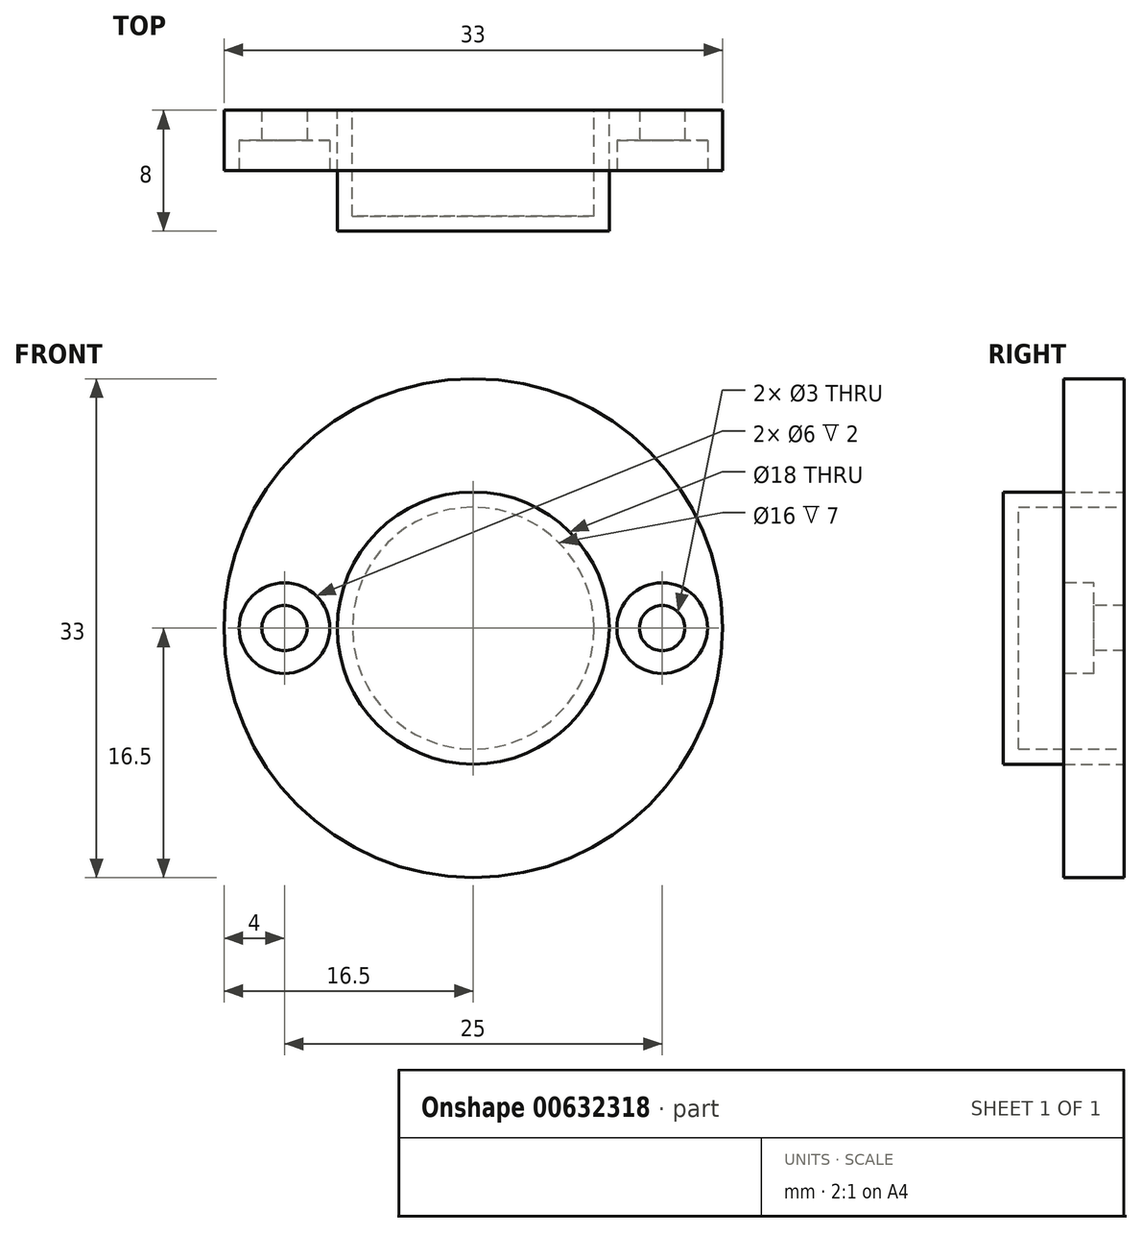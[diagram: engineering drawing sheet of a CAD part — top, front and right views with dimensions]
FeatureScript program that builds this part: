
annotation { "Feature Type Name" : "Feature", "Feature Type Description" : "" }
export const myFeature = defineFeature(function(context is Context, id is Id, definition is map)
    precondition{}
    {
        {
            var Q0;
            Q0=qCreatedBy(makeId("Front.planeOp"),FACE);
            var sketch = newSketch(context, id + "F0", { "sketchPlane" : qUnion([Q0])});
            skCircle(sketch, "E0", {"center": v(0, 0) * mm, "radius": 16.5 * mm});
            skPoint(sketch, "E1", {"position": v(-12.5, 0) * mm});
            skPoint(sketch, "E2", {"position": v(12.5, 0) * mm});
            skCircle(sketch, "E3", {"center": v(0, 0) * mm, "radius": 9 * mm});
            skSolve(sketch);
        }
        {
            var Q0;
            Q0=makeQuery(id+"F0.imprint","IMPRINT",FACE,{"disambiguationData":[TD([[makeQuery(id+"F0.imprint","IMPRINT",EDGE,{"derivedFrom":sQuery(id+"F0.wireOp",EDGE,"E3")}),1.0]])]});
            var Q1;
            Q1=sQuery(id+"F0.wireOp",EDGE,"E3");
            extrude(context, id + "F1", {"entities" : qUnion([Q0]), "surfaceEntities" : qUnion([Q1]), "depth" : 8 * mm, "offsetDistance" : 25 * mm});
        }
        {
            var Q0;
            Q0=makeQuery(id+"F0.imprint","IMPRINT",FACE,{"disambiguationData":[TD([[makeQuery(id+"F0.imprint","IMPRINT",EDGE,{"derivedFrom":sQuery(id+"F0.wireOp",EDGE,"E0")}),1.0]])]});
            var Q1;
            Q1=sQuery(id+"F0.wireOp",EDGE,"E0");
            extrude(context, id + "F2", {"entities" : qUnion([Q0]), "surfaceEntities" : qUnion([Q1]), "depth" : 4 * mm, "offsetDistance" : 25 * mm});
        }
        {
            var Q0;
            Q0=makeQuery(id+"F1.opExtrude","CAP_FACE",FACE,{"disambiguationData":[OSD([sQuery(id+"F0.wireOp",EDGE,"E3")])],"isStart":true});
            shell(context, id + "F3", {"entities" : qUnion([Q0]), "thickness" : 1 * mm});
        }
        {
            var Q0;
            Q0=makeQuery(id+"F2.opExtrude","SWEPT_BODY",BODY,{"disambiguationData":[OSD([sQuery(id+"F0.wireOp",EDGE,"E0"),sQuery(id+"F0.wireOp",EDGE,"E3")])]});
            var Q1;
            Q1=makeQuery(id+"F1.opExtrude","SWEPT_BODY",BODY,{"disambiguationData":[OSD([sQuery(id+"F0.wireOp",EDGE,"E3")])]});
            var Q2;
            Q2=qCreatedBy(makeId("Front.planeOp"),FACE);
            var Q3;
            Q3=makeQuery(id+"F2.opExtrude","SWEPT_FACE",FACE,{"disambiguationData":[OSD([sQuery(id+"F0.wireOp",EDGE,"E0")])]});
            transform(context, id + "F4", {"entities" : qUnion([Q0, Q1]), "transformType" : TransformType.TRANSLATION_DISTANCE, "transformDirection" : qUnion([Q2, Q3]), "distance" : 4 * mm, "oppositeDirection" : true, "makeCopy" : false});
        }
        {
            var Q0;
            Q0=sQuery(id+"F0.wireOp",VERTEX,"E1");
            var Q1;
            Q1=sQuery(id+"F0.wireOp",VERTEX,"E2");
            var Q2;
            Q2=makeQuery(id+"F2.opExtrude","SWEPT_BODY",BODY,{"disambiguationData":[OSD([sQuery(id+"F0.wireOp",EDGE,"E0"),sQuery(id+"F0.wireOp",EDGE,"E3")])]});
            hole(context, id + "F5", {"style" : HoleStyle.C_BORE, "endStyle" : HoleEndStyle.THROUGH, "holeDiameter" : 3 * mm, "cBoreDiameter" : 6 * mm, "cBoreDepth" : 2 * mm, "majorDiameter" : 5 * mm, "isTappedThrough" : true, "tappedDepth" : 12 * mm, "tapClearance" : 3, "startFromSketch" : true, "locations" : qUnion([Q0, Q1]), "scope" : qUnion([Q2])});
        }
    });
